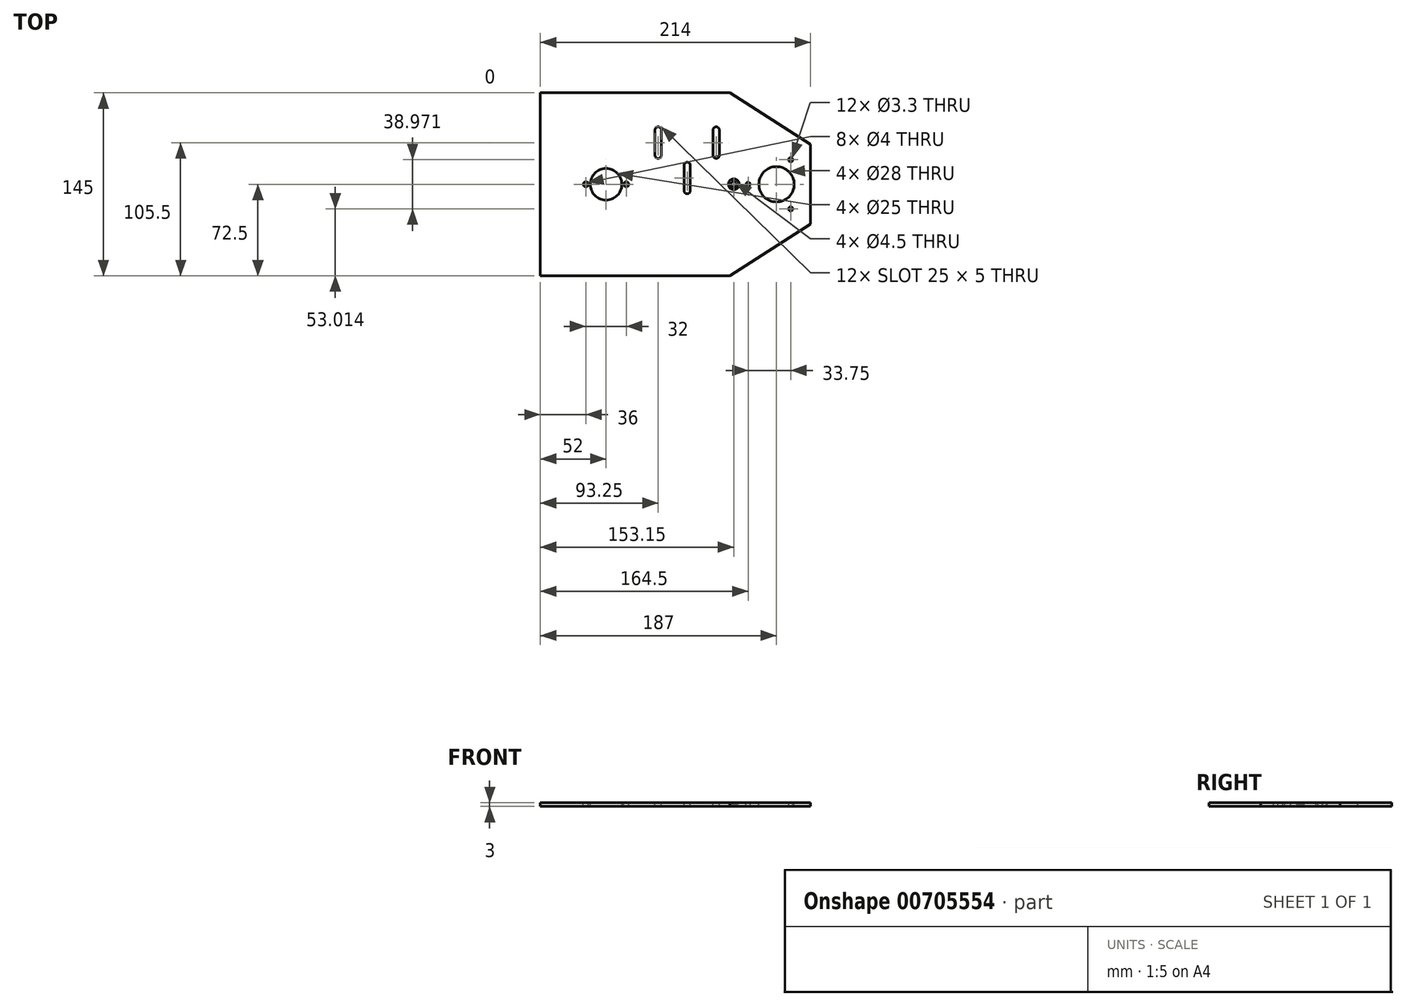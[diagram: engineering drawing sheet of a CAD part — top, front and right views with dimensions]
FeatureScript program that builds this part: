
annotation { "Feature Type Name" : "Feature", "Feature Type Description" : "" }
export const myFeature = defineFeature(function(context is Context, id is Id, definition is map)
    precondition{}
    {
        {
            var Q0;
            Q0=qCreatedBy(makeId("Top.planeOp"),FACE);
            var sketch = newSketch(context, id + "F0", { "sketchPlane" : qUnion([Q0])});
            skLineSegment(sketch, "E0.bottom", {"start": v(75, 72.5) * mm, "end": v(-75, 72.5) * mm});
            skLineSegment(sketch, "E0.top", {"start": v(75, -72.5) * mm, "end": v(-75, -72.5) * mm});
            skLineSegment(sketch, "E0.left", {"start": v(75, 72.5) * mm, "end": v(75, -72.5) * mm});
            skLineSegment(sketch, "E0.right", {"start": v(-75, 72.5) * mm, "end": v(-75, -72.5) * mm});
            skPoint(sketch, "E0.middle", {"position": v(0, 0) * mm});
            skLineSegment(sketch, "E1", {"start": v(75, 0) * mm, "end": v(139, 0) * mm});
            skLineSegment(sketch, "E2", {"start": v(139, 31.5) * mm, "end": v(139, 0) * mm});
            skLineSegment(sketch, "E3", {"start": v(75, 72.5) * mm, "end": v(139, 31.5) * mm});
            skLineSegment(sketch, "E4.MirrorCS", {"start": v(75, -72.5) * mm, "end": v(139, -31.5) * mm});
            skLineSegment(sketch, "E5.MirrorCS", {"start": v(139, -31.5) * mm, "end": v(139, 0) * mm});
            skSolve(sketch);
        }
        {
            var Q0;
            Q0 = qSketchRegion(id + "F0", true);
            extrude(context, id + "F1", {"entities" : qUnion([Q0]), "depth" : 3 * mm, "offsetDistance" : 25 * mm});
        }
        {
            var Q0;
            Q0=makeQuery(id+"F1.opExtrude","CAP_FACE",FACE,{"disambiguationData":[OSD([sQuery(id+"F0.wireOp",EDGE,"E0.bottom"),sQuery(id+"F0.wireOp",EDGE,"E0.top"),sQuery(id+"F0.wireOp",EDGE,"E0.right"),sQuery(id+"F0.wireOp",EDGE,"E2"),sQuery(id+"F0.wireOp",EDGE,"E3"),sQuery(id+"F0.wireOp",EDGE,"E4.MirrorCS"),sQuery(id+"F0.wireOp",EDGE,"E5.MirrorCS")])],"isStart":false});
            var sketch = newSketch(context, id + "F2", { "sketchPlane" : qUnion([Q0])});
            skLineSegment(sketch, "E6", {"start": v(139, 31.5) * mm, "end": v(139, -31.5) * mm});
            skLineSegment(sketch, "E7.0", {"start": v(112, 31.5) * mm, "end": v(112, -31.5) * mm});
            skLineSegment(sketch, "E8", {"start": v(139, 0) * mm, "end": v(112, 0) * mm});
            skCircle(sketch, "E9", {"center": v(112, 0) * mm, "radius": 12.5 * mm});
            skSolve(sketch);
        }
        {
            var Q0;
            Q0=sQuery(id+"F2.wireOp",VERTEX,"E9.center");
            var Q1;
            Q1=makeQuery(id+"F1.opExtrude","SWEPT_BODY",BODY,{"disambiguationData":[OSD([sQuery(id+"F0.wireOp",EDGE,"E0.bottom"),sQuery(id+"F0.wireOp",EDGE,"E0.top"),sQuery(id+"F0.wireOp",EDGE,"E0.right"),sQuery(id+"F0.wireOp",EDGE,"E2"),sQuery(id+"F0.wireOp",EDGE,"E3"),sQuery(id+"F0.wireOp",EDGE,"E4.MirrorCS"),sQuery(id+"F0.wireOp",EDGE,"E5.MirrorCS")])]});
            hole(context, id + "F3", {"style" : HoleStyle.SIMPLE, "endStyle" : HoleEndStyle.THROUGH, "holeDiameter" : 28 * mm, "majorDiameter" : 5 * mm, "isTappedThrough" : true, "tappedDepth" : 12 * mm, "tapClearance" : 3, "locations" : qUnion([Q0]), "scope" : qUnion([Q1])});
        }
        {
            var Q0;
            Q0=makeQuery(id+"F1.opExtrude","CAP_FACE",FACE,{"disambiguationData":[OSD([sQuery(id+"F0.wireOp",EDGE,"E0.bottom"),sQuery(id+"F0.wireOp",EDGE,"E0.top"),sQuery(id+"F0.wireOp",EDGE,"E0.right"),sQuery(id+"F0.wireOp",EDGE,"E2"),sQuery(id+"F0.wireOp",EDGE,"E3"),sQuery(id+"F0.wireOp",EDGE,"E4.MirrorCS"),sQuery(id+"F0.wireOp",EDGE,"E5.MirrorCS")])],"isStart":false});
            var sketch = newSketch(context, id + "F4", { "sketchPlane" : qUnion([Q0])});
            skCircle(sketch, "E10", {"center": v(112, 0) * mm, "radius": 22.5 * mm});
            skLineSegment(sketch, "E11", {"start": v(112, 0) * mm, "end": v(89.5, 0) * mm});
            skCircle(sketch, "E12", {"center": v(89.5, 0) * mm, "radius": 1.75 * mm});
            skCircle(sketch, "E13.1.0", {"center": v(123.25, -19.49) * mm, "radius": 1.75 * mm});
            skCircle(sketch, "E13.2.0", {"center": v(123.25, 19.49) * mm, "radius": 1.75 * mm});
            skSolve(sketch);
        }
        {
            var Q0;
            Q0=sQuery(id+"F4.wireOp",VERTEX,"E12.center");
            var Q1;
            Q1=sQuery(id+"F4.wireOp",VERTEX,"E13.1.0.center");
            var Q2;
            Q2=sQuery(id+"F4.wireOp",VERTEX,"E13.2.0.center");
            var Q3;
            Q3=makeQuery(id+"F1.opExtrude","SWEPT_BODY",BODY,{"disambiguationData":[OSD([sQuery(id+"F0.wireOp",EDGE,"E0.bottom"),sQuery(id+"F0.wireOp",EDGE,"E0.top"),sQuery(id+"F0.wireOp",EDGE,"E0.right"),sQuery(id+"F0.wireOp",EDGE,"E2"),sQuery(id+"F0.wireOp",EDGE,"E3"),sQuery(id+"F0.wireOp",EDGE,"E4.MirrorCS"),sQuery(id+"F0.wireOp",EDGE,"E5.MirrorCS")])]});
            hole(context, id + "F5", {"style" : HoleStyle.SIMPLE, "endStyle" : HoleEndStyle.THROUGH, "standardTappedOrClearance" : lookupTablePath({ "standard" : "ISO", "fit" : "Normal", "size" : "M3", "type" : "Clearance" }), "standardBlindInLast" : lookupTablePath({ "fit" : "Standard", "standard" : "ISO", "size" : "M3", "type" : "Clearance" }), "holeDiameter" : 3.3 * mm, "majorDiameter" : 5 * mm, "isTappedThrough" : true, "tappedDepth" : 12 * mm, "tapClearance" : 3, "locations" : qUnion([Q0, Q1, Q2]), "scope" : qUnion([Q3])});
        }
        {
            var Q0;
            Q0=makeQuery(id+"F1.opExtrude","CAP_FACE",FACE,{"disambiguationData":[OSD([sQuery(id+"F0.wireOp",EDGE,"E0.bottom"),sQuery(id+"F0.wireOp",EDGE,"E0.top"),sQuery(id+"F0.wireOp",EDGE,"E0.right"),sQuery(id+"F0.wireOp",EDGE,"E2"),sQuery(id+"F0.wireOp",EDGE,"E3"),sQuery(id+"F0.wireOp",EDGE,"E4.MirrorCS"),sQuery(id+"F0.wireOp",EDGE,"E5.MirrorCS")])],"isStart":false});
            var sketch = newSketch(context, id + "F6", { "sketchPlane" : qUnion([Q0])});
            skLineSegment(sketch, "E14", {"start": v(112, 0) * mm, "end": v(112, -36.09) * mm, "construction": true});
            skLineSegment(sketch, "E15.0", {"start": v(-23, 72.5) * mm, "end": v(-23, -36.09) * mm, "construction": true});
            skLineSegment(sketch, "E16.0", {"start": v(-39, 0) * mm, "end": v(-39, -36.09) * mm});
            skLineSegment(sketch, "E17.0", {"start": v(-7, 0) * mm, "end": v(-7, -36.09) * mm});
            skLineSegment(sketch, "E18", {"start": v(-7, 0) * mm, "end": v(-39, 0) * mm});
            skCircle(sketch, "E19", {"center": v(-39, 0) * mm, "radius": 2 * mm});
            skCircle(sketch, "E20", {"center": v(-7, 0) * mm, "radius": 2 * mm});
            skCircle(sketch, "E21", {"center": v(-23, 0) * mm, "radius": 12.5 * mm});
            skSolve(sketch);
        }
        {
            var Q0;
            Q0 = qSketchRegion(id + "F6", true);
            extrude(context, id + "F7", {"entities" : qUnion([Q0]), "operationType" : NewBodyOperationType.REMOVE, "endBound" : BoundingType.UP_TO_NEXT, "oppositeDirection" : true, "depth" : 25 * mm, "offsetDistance" : 25 * mm});
        }
        {
            var Q0;
            Q0=makeQuery(id+"F1.opExtrude","CAP_FACE",FACE,{"disambiguationData":[OSD([sQuery(id+"F0.wireOp",EDGE,"E0.bottom"),sQuery(id+"F0.wireOp",EDGE,"E0.top"),sQuery(id+"F0.wireOp",EDGE,"E0.right"),sQuery(id+"F0.wireOp",EDGE,"E2"),sQuery(id+"F0.wireOp",EDGE,"E3"),sQuery(id+"F0.wireOp",EDGE,"E4.MirrorCS"),sQuery(id+"F0.wireOp",EDGE,"E5.MirrorCS")])],"isStart":false});
            var sketch = newSketch(context, id + "F8", { "sketchPlane" : qUnion([Q0])});
            skLineSegment(sketch, "E22", {"start": v(-7, 0) * mm, "end": v(89.5, 0) * mm, "construction": true});
            skLineSegment(sketch, "E23", {"start": v(41.25, 0) * mm, "end": v(41.25, 72.5) * mm, "construction": true});
            skLineSegment(sketch, "E24.0", {"start": v(-7, -5) * mm, "end": v(69.5, -5) * mm, "construction": true});
            skLineSegment(sketch, "E25.0", {"start": v(-7, 15) * mm, "end": v(69.5, 15) * mm, "construction": true});
            skArc(sketch, "E26", {"start": v(38.75, -5) * mm, "mid": v(41.25, -7.5) * mm, "end": v(43.75, -5) * mm});
            skArc(sketch, "E27", {"start": v(43.75, 15) * mm, "mid": v(41.25, 17.5) * mm, "end": v(38.75, 15) * mm});
            skLineSegment(sketch, "E28", {"start": v(38.75, 15) * mm, "end": v(38.75, -5) * mm});
            skLineSegment(sketch, "E29", {"start": v(43.75, 15) * mm, "end": v(43.75, -5) * mm});
            skLineSegment(sketch, "E30.0", {"start": v(64.25, 0) * mm, "end": v(64.25, 72.5) * mm});
            skLineSegment(sketch, "E31.0", {"start": v(-7, 23) * mm, "end": v(69.5, 23) * mm, "construction": true});
            skLineSegment(sketch, "E32.0", {"start": v(-7, 43) * mm, "end": v(69.5, 43) * mm, "construction": true});
            skArc(sketch, "E33", {"start": v(66.75, 43) * mm, "mid": v(64.25, 45.5) * mm, "end": v(61.75, 43) * mm});
            skArc(sketch, "E34", {"start": v(61.75, 23) * mm, "mid": v(64.25, 20.5) * mm, "end": v(66.75, 23) * mm});
            skLineSegment(sketch, "E35", {"start": v(61.75, 43) * mm, "end": v(61.75, 23) * mm});
            skLineSegment(sketch, "E36", {"start": v(66.75, 43) * mm, "end": v(66.75, 23) * mm});
            skLineSegment(sketch, "E37.MirrorCS", {"start": v(20.75, 43) * mm, "end": v(20.75, 23) * mm});
            skArc(sketch, "E38.MirrorCS", {"start": v(15.75, 43) * mm, "mid": v(18.25, 45.5) * mm, "end": v(20.75, 43) * mm});
            skLineSegment(sketch, "E39.MirrorCS", {"start": v(15.75, 43) * mm, "end": v(15.75, 23) * mm});
            skArc(sketch, "E40.MirrorCS", {"start": v(20.75, 23) * mm, "mid": v(18.25, 20.5) * mm, "end": v(15.75, 23) * mm});
            skSolve(sketch);
        }
        {
            var Q0;
            Q0 = qSketchRegion(id + "F8", true);
            extrude(context, id + "F9", {"entities" : qUnion([Q0]), "operationType" : NewBodyOperationType.REMOVE, "endBound" : BoundingType.UP_TO_NEXT, "oppositeDirection" : true, "depth" : 25 * mm, "offsetDistance" : 25 * mm});
        }
        {
            var Q0;
            Q0=makeQuery(id+"F1.opExtrude","CAP_FACE",FACE,{"disambiguationData":[OSD([sQuery(id+"F0.wireOp",EDGE,"E0.bottom"),sQuery(id+"F0.wireOp",EDGE,"E0.top"),sQuery(id+"F0.wireOp",EDGE,"E0.right"),sQuery(id+"F0.wireOp",EDGE,"E2"),sQuery(id+"F0.wireOp",EDGE,"E3"),sQuery(id+"F0.wireOp",EDGE,"E4.MirrorCS"),sQuery(id+"F0.wireOp",EDGE,"E5.MirrorCS")])],"isStart":false});
            var sketch = newSketch(context, id + "F10", { "sketchPlane" : qUnion([Q0])});
            skLineSegment(sketch, "E41", {"start": v(84.16, -29.37) * mm, "end": v(84.16, 40.6) * mm, "construction": true});
            skLineSegment(sketch, "E42.0", {"start": v(78.15, -29.37) * mm, "end": v(78.15, 40.6) * mm, "construction": true});
            skLineSegment(sketch, "E43", {"start": v(-9, 0) * mm, "end": v(87.85, 0) * mm, "construction": true});
            skCircle(sketch, "E44", {"center": v(78.15, 0) * mm, "radius": 3.27 * mm});
            skSolve(sketch);
        }
        {
            var Q0;
            Q0=sQuery(id+"F10.wireOp",VERTEX,"E44.center");
            var Q1;
            Q1=makeQuery(id+"F1.opExtrude","SWEPT_BODY",BODY,{"disambiguationData":[OSD([sQuery(id+"F0.wireOp",EDGE,"E0.bottom"),sQuery(id+"F0.wireOp",EDGE,"E0.top"),sQuery(id+"F0.wireOp",EDGE,"E0.right"),sQuery(id+"F0.wireOp",EDGE,"E2"),sQuery(id+"F0.wireOp",EDGE,"E3"),sQuery(id+"F0.wireOp",EDGE,"E4.MirrorCS"),sQuery(id+"F0.wireOp",EDGE,"E5.MirrorCS")])]});
            hole(context, id + "F11", {"style" : HoleStyle.C_SINK, "endStyle" : HoleEndStyle.THROUGH, "holeDiameter" : 4.5 * mm, "cSinkDiameter" : 8.5 * mm, "cSinkAngle" : 90 * degree, "majorDiameter" : 5 * mm, "isTappedThrough" : true, "tappedDepth" : 12 * mm, "tapClearance" : 3, "locations" : qUnion([Q0]), "scope" : qUnion([Q1])});
        }
    });
